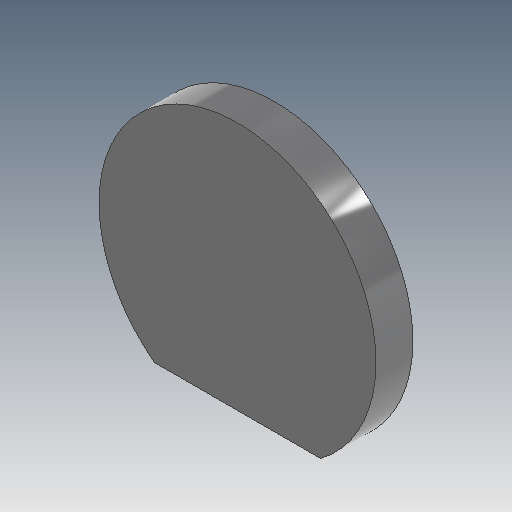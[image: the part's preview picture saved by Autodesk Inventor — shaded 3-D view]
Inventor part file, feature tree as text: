
AUTODESK INVENTOR PART (.ipt)
format: ipt  version: 2020.3 (Build 243373010, 373A)  size: 92,672 bytes
history: native  units: mm
features: extrude x1, sketch x1
ambient origin geometry x8: Origin, YZ Plane, XZ Plane, XY Plane, X Axis, Y Axis, Z Axis, Center Point
bodies: Solid1 (feature_tree)
feature tree (2):
  extrude  "Extrusion1"  Depth=4.0mm
  sketch  "Sketch1"  dims[d0=30.0mm d1=12.0mm d2=4.0mm d3=0.0mm]
